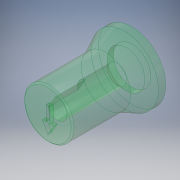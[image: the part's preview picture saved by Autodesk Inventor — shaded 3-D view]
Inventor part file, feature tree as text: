
AUTODESK INVENTOR PART (.ipt)
format: ipt  version: 2017 SP1 (Build 210196100, 196)  size: 176,640 bytes
history: native  units: in
note: dims shown in document units (in); Inventor stores cm internally (conversion verified against a paired STEP export)
features: extrude x6, sketch x6, chamfer x3, projected_geometry x1
ambient origin geometry x8: Origin, YZ Plane, XZ Plane, XY Plane, X Axis, Y Axis, Z Axis, Center Point
bodies: Solid1 (feature_tree)
feature tree (16):
  extrude  "Extrusion1"  Depth=0.0125in
  extrude  "Extrusion2"  Depth=0.2in
  extrude  "Extrusion3"  Depth=0.2in
  chamfer  "Chamfer1"  Distance=0.05in
  extrude  "Extrusion6"  TaperAngle=60.0deg  [1 undecoded]
  extrude  "Extrusion10"  Depth=0.05in
  chamfer  "Chamfer3"  Distance=0.4in
  extrude  "Extrusion11"  Depth=0.05in
  chamfer  "Chamfer4"  Distance=0.5in
  sketch  "Sketch1"  dims[d0=0.235in d2=0.0125in]
  sketch  "Sketch2"  dims[d3=1.0in d4=0.0in d5=0.2in]
  sketch  "Sketch3"  dims[d6=0.125in d7=0.0in d8=0.2in]
  sketch  "Sketch6"  dims[d10=0.05in]
  projected_geometry  "Projected Loop4"
  sketch  "Sketch10"  dims[d11=0.15in d12=0.05in d13=0.0in]
  sketch  "Sketch11"  dims[d20=0.02in d21=0.125in d22=45.0deg d24=60.0deg d26=0.215in d27=0.4in d28=0.0in d45=0.1333in d49=0.5in d50=0.2in d51=0.2in d52=0.1in d53=0.0in d54=0.25in d55=0.12in d56=45.0deg d57=0.5in d58=0.2in d59=0.0in d60=0.12in d61=0.05in d62=45.0deg]
note: 1 required parameter value undecoded (feature->parameter linkage not recoverable at this tier; creation-order binding heuristic only, values carry confidence <= 0.55)
